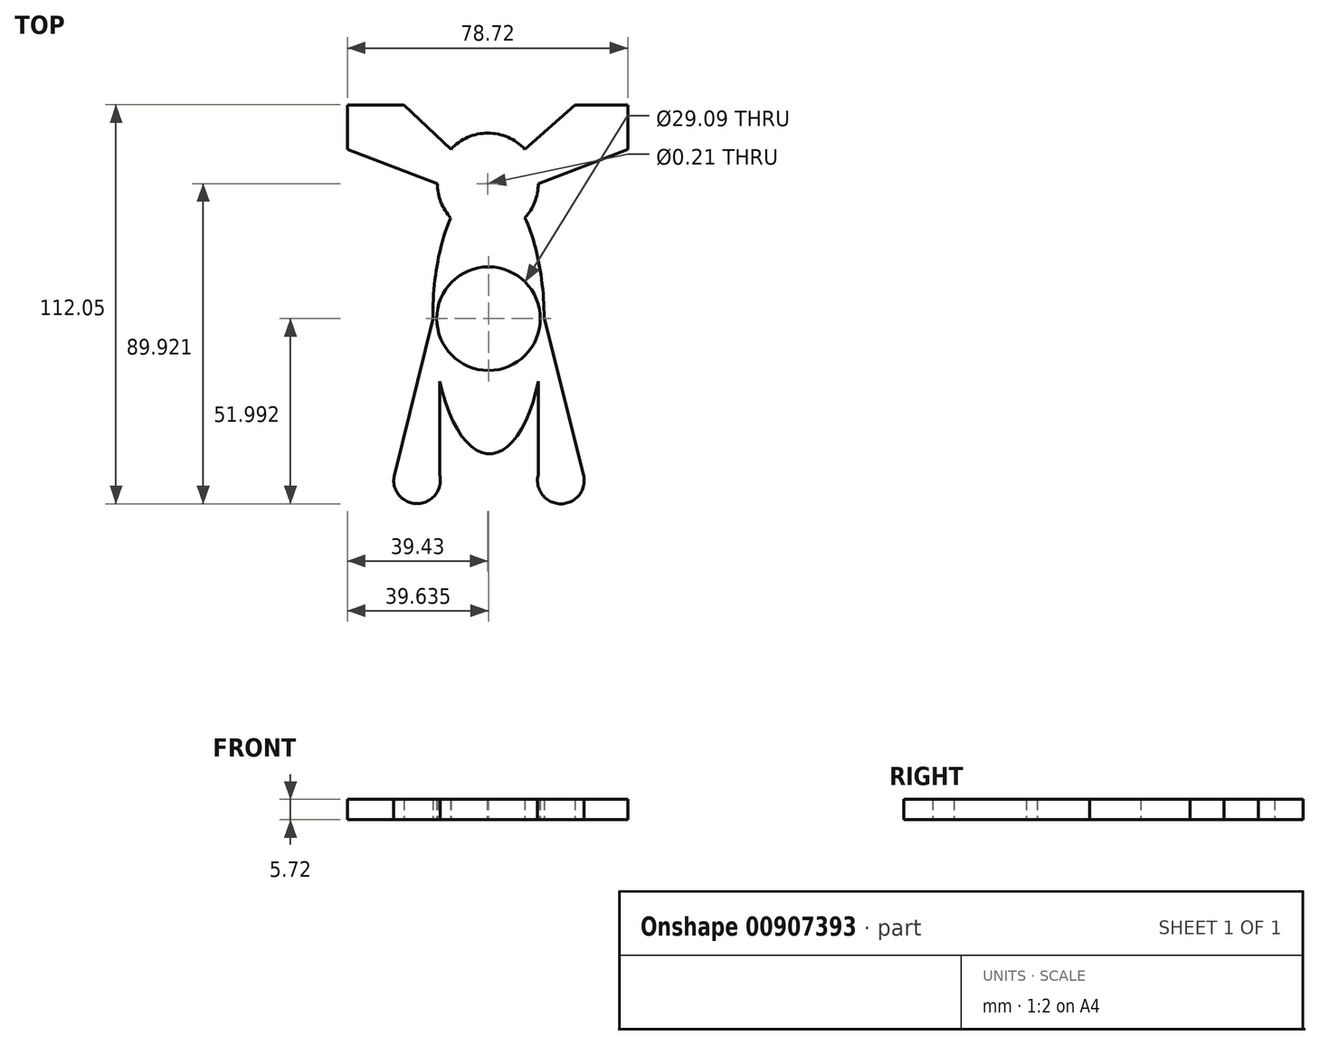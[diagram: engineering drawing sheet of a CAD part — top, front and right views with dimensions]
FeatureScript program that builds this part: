
annotation { "Feature Type Name" : "Feature", "Feature Type Description" : "" }
export const myFeature = defineFeature(function(context is Context, id is Id, definition is map)
    precondition{}
    {
        {
            var Q0;
            Q0=qCreatedBy(makeId("Top.planeOp"),FACE);
            var sketch = newSketch(context, id + "F0", { "sketchPlane" : qUnion([Q0])});
            skEllipse(sketch, "E0", {"center": v(-3.6, -1.3) * mm, "majorRadius": 37.93 * mm, "minorRadius": 15.63 * mm, "majorAxis": v(0, -1)});
            skLineSegment(sketch, "E1", {"start": v(10.36, -18.91) * mm, "end": v(10.36, -45.15) * mm});
            skLineSegment(sketch, "E2", {"start": v(-17.33, -18.91) * mm, "end": v(-17.33, -45.15) * mm});
            skLineSegment(sketch, "E3", {"start": v(-17.33, -45.15) * mm, "end": v(-30.03, -45.15) * mm});
            skLineSegment(sketch, "E4", {"start": v(-30.03, -45.15) * mm, "end": v(-19.24, -1.43) * mm});
            skLineSegment(sketch, "E5", {"start": v(10.36, -45.15) * mm, "end": v(23.06, -45.15) * mm});
            skLineSegment(sketch, "E6", {"start": v(23.06, -45.15) * mm, "end": v(12.03, -1.17) * mm});
            skArc(sketch, "E7", {"start": v(10.36, -45.15) * mm, "mid": v(16.71, -53.29) * mm, "end": v(23.06, -45.15) * mm});
            skArc(sketch, "E8", {"start": v(-30.03, -45.15) * mm, "mid": v(-23.68, -53.25) * mm, "end": v(-17.33, -45.15) * mm});
            skCircle(sketch, "E9", {"center": v(-3.81, 36.63) * mm, "radius": 14.17 * mm});
            skPoint(sketch, "E9.centerSnap0", {"position": v(-3.92, 36.63) * mm});
            skLineSegment(sketch, "E10", {"start": v(6.56, 46.3) * mm, "end": v(20.7, 58.76) * mm});
            skLineSegment(sketch, "E11", {"start": v(20.7, 58.76) * mm, "end": v(35.48, 58.76) * mm});
            skLineSegment(sketch, "E12", {"start": v(35.48, 58.76) * mm, "end": v(35.48, 46.3) * mm});
            skLineSegment(sketch, "E13", {"start": v(35.48, 46.3) * mm, "end": v(10.36, 36.63) * mm});
            skLineSegment(sketch, "E14", {"start": v(-14.18, 46.3) * mm, "end": v(-27.35, 58.76) * mm});
            skLineSegment(sketch, "E15", {"start": v(-27.35, 58.76) * mm, "end": v(-43.24, 58.76) * mm});
            skLineSegment(sketch, "E16", {"start": v(-43.24, 58.76) * mm, "end": v(-43.24, 46.3) * mm});
            skLineSegment(sketch, "E17", {"start": v(-43.24, 46.3) * mm, "end": v(-17.98, 36.63) * mm});
            skCircle(sketch, "E18", {"center": v(-3.81, 36.63) * mm, "radius": 0.1 * mm});
            skCircle(sketch, "E19", {"center": v(-3.6, -1.3) * mm, "radius": 11.05 * mm});
            skCircle(sketch, "E20", {"center": v(-3.6, -1.3) * mm, "radius": 14.55 * mm});
            skSolve(sketch);
        }
        {
            var Q0;
            Q0=makeQuery(id+"F0.imprint","IMPRINT",FACE,{"disambiguationData":[TD([[makeQuery(id+"F0.imprint","IMPRINT",EDGE,{"derivedFrom":sQuery(id+"F0.wireOp",EDGE,"E20")}),-1.0]])]});
            extrude(context, id + "F1", {"entities" : qUnion([Q0]), "depth" : 3.17 * mm, "offsetDistance" : 25.4 * mm});
        }
        {
            var Q0;
            Q0 = qSketchRegion(id + "F0", true);
            extrude(context, id + "F2", {"entities" : qUnion([Q0]), "operationType" : NewBodyOperationType.ADD, "depth" : 5.7 * mm, "offsetDistance" : 25.4 * mm});
        }
    });
